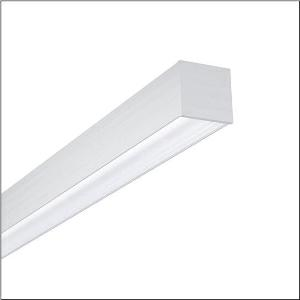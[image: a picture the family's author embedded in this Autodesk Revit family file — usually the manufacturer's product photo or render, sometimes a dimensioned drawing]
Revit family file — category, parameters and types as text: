
# Revit family: silica_r_5mx31bd1e4a_96a8
name_source: partatom
category: Lighting Fixtures
units: mm (PartAtom-declared; Revit-internal decimal feet)

## family parameters
Cut with Voids When Loaded = No
Host = Face
Light Source = No
Part Type = Normal
Room Calculation Point = No
Round Connector Dimension = Use Diameter
Shared = No

## types (1)
- --- (1 x LED, 7070 lm, 45.6 W, 4000K)
    Apparent Load = 46 VA
    CIE Flux Codes = 82 97 100 70 100
    Color Rendering = 80
    Color Temperature = 4000K
    Default Elevation = 1800 mm
    Description = Silica®, office luminaire, of aluminium, light emission: direct/indirect distribution, primary light characteristic: symmetric, installation type: suspended mounting, LED, rated luminous flux: 7.070lm, luminous efficacy: 155lm/W, light colour: 840, colour temperature: 4000K, control gear: DALI (with two DALI addresses), with terminal, 3+2-pole, max. 2.5mm², mains connection: 230V, AC, 50/60Hz, connection cable inclusive, cable length: 1,5m, rated input power: 46W, luminaire housing, of aluminium, anodised, silver, length: 1.442mm, width: 65mm, height: 64mm, protection rating (complete): IP20, insulation class (complete): insulation class I (protective earthing), certification: CE, permissible operating ambient temperature: 0..+35°C, standard: EN 50419, packaging unit: 1 piece
    Height = 64 mm
    Lamp = 1 x LED
    Lamp Light Flux = 7070 lm
    Lamp Power = 45.6 W
    Lamp count = 1
    Length = 1442 mm
    Luminous efficacy = 155 lm/W
    Manufacturer = Siteco
    ModVariant = No
    Model = 5MX31BD1E4A
    Mounting Place = Ceiling
    Mounting Type = Pendant
    Number of Poles = 1
    OnlyDefault = Yes
    Power Factor = 1
    Product Name = Silica®
    Product group = office luminaire | ceiling pendant
    ProductGroupID = 904
    Protection Class = Protection class I
    Protection Degree = IP 20
    RLX_Detail_Level = 1
    RLX_Emergency_Light_Flux = 0 lm
    RLX_Emergency_Type = 0
    RLX_Emergency_Type_DB = No
    RlxData = <blob elided: 32761 chars, md5=321b8578>
    Socket = socket
    Standby Power = 0 W
    System Light Flux = 7070 lm
    System Power = 46 W
    Type Comments = factory setting: direct and indirect light
    Type Image = l_1005409.jpg
    URL = http://relux.com
    VarID = @adj_198507
    Voltage = 0 V
    Weight = 0.00 kg
    Width = 66 mm

## geometry (parser evidence)
native form markers: Blend x4, Sweep x10
no freeform markers — native parametric forms only
